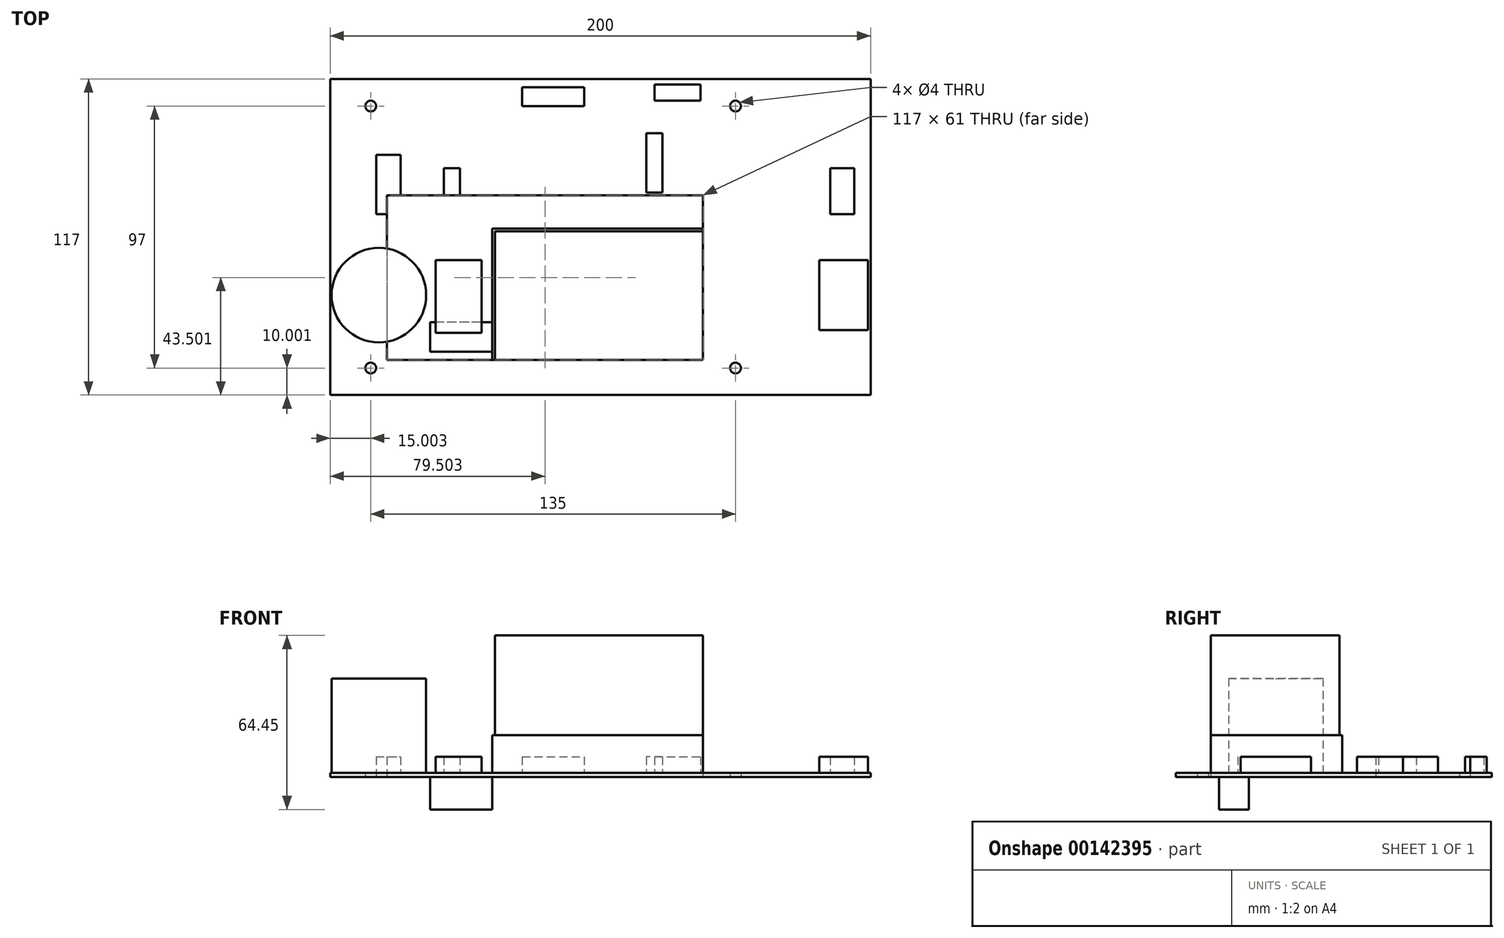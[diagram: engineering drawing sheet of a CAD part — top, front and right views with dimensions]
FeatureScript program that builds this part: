
annotation { "Feature Type Name" : "Feature", "Feature Type Description" : "" }
export const myFeature = defineFeature(function(context is Context, id is Id, definition is map)
    precondition{}
    {
        {
            var Q0;
            Q0=qCreatedBy(makeId("Top.planeOp"),FACE);
            var sketch = newSketch(context, id + "F0", { "sketchPlane" : qUnion([Q0])});
            skLineSegment(sketch, "E0.bottom", {"start": v(-88.8, 43.67) * mm, "end": v(111.2, 43.67) * mm});
            skLineSegment(sketch, "E0.top", {"start": v(-88.8, -73.33) * mm, "end": v(111.2, -73.33) * mm});
            skLineSegment(sketch, "E0.left", {"start": v(-88.8, 43.67) * mm, "end": v(-88.8, -73.33) * mm});
            skLineSegment(sketch, "E0.right", {"start": v(111.2, 43.67) * mm, "end": v(111.2, -73.33) * mm});
            skCircle(sketch, "E1", {"center": v(61.2, 33.67) * mm, "radius": 2 * mm});
            skCircle(sketch, "E2", {"center": v(61.2, -63.33) * mm, "radius": 2 * mm});
            skCircle(sketch, "E3", {"center": v(-73.8, -63.33) * mm, "radius": 2 * mm});
            skCircle(sketch, "E4", {"center": v(-73.8, 33.67) * mm, "radius": 2 * mm});
            skLineSegment(sketch, "E5.bottom", {"start": v(-67.8, 0.67) * mm, "end": v(49.2, 0.67) * mm});
            skLineSegment(sketch, "E5.top", {"start": v(-67.8, -60.33) * mm, "end": v(49.2, -60.33) * mm});
            skLineSegment(sketch, "E5.left", {"start": v(-67.8, 0.67) * mm, "end": v(-67.8, -60.33) * mm});
            skLineSegment(sketch, "E5.right", {"start": v(49.2, 0.67) * mm, "end": v(49.2, -60.33) * mm});
            skSolve(sketch);
        }
        {
            var Q0;
            Q0 = qSketchRegion(id + "F0", true);
            extrude(context, id + "F1", {"entities" : qUnion([Q0]), "depth" : 1.5 * mm});
        }
        {
            var Q0;
            Q0=makeQuery(id+"F1.opExtrude","CAP_FACE",FACE,{"disambiguationData":[OSD([sQuery(id+"F0.wireOp",EDGE,"E0.bottom"),sQuery(id+"F0.wireOp",EDGE,"E0.top"),sQuery(id+"F0.wireOp",EDGE,"E0.left"),sQuery(id+"F0.wireOp",EDGE,"E0.right"),sQuery(id+"F0.wireOp",EDGE,"E1"),sQuery(id+"F0.wireOp",EDGE,"E2"),sQuery(id+"F0.wireOp",EDGE,"E3"),sQuery(id+"F0.wireOp",EDGE,"E4")])],"isStart":false});
            var sketch = newSketch(context, id + "F2", { "sketchPlane" : qUnion([Q0])});
            skLineSegment(sketch, "E6.bottom", {"start": v(-17.8, 40.67) * mm, "end": v(5.2, 40.67) * mm});
            skLineSegment(sketch, "E6.top", {"start": v(-17.8, 33.67) * mm, "end": v(5.2, 33.67) * mm});
            skLineSegment(sketch, "E6.left", {"start": v(5.2, 40.67) * mm, "end": v(5.2, 33.67) * mm});
            skLineSegment(sketch, "E6.right", {"start": v(-17.8, 40.67) * mm, "end": v(-17.8, 33.67) * mm});
            skLineSegment(sketch, "E7.bottom", {"start": v(31.2, 41.67) * mm, "end": v(48.2, 41.67) * mm});
            skLineSegment(sketch, "E7.top", {"start": v(31.2, 35.67) * mm, "end": v(48.2, 35.67) * mm});
            skLineSegment(sketch, "E7.left", {"start": v(31.2, 41.67) * mm, "end": v(31.2, 35.67) * mm});
            skLineSegment(sketch, "E7.right", {"start": v(48.2, 41.67) * mm, "end": v(48.2, 35.67) * mm});
            skLineSegment(sketch, "E8.top", {"start": v(34.2, 1.67) * mm, "end": v(28.2, 1.67) * mm});
            skLineSegment(sketch, "E8.left", {"start": v(28.2, 23.67) * mm, "end": v(28.2, 1.67) * mm});
            skLineSegment(sketch, "E9", {"start": v(34.2, 23.67) * mm, "end": v(34.2, 1.67) * mm});
            skPoint(sketch, "E10.orphan", {"position": v(0, 1.67) * mm});
            skLineSegment(sketch, "E11", {"start": v(28.2, 23.67) * mm, "end": v(34.2, 23.67) * mm});
            skPoint(sketch, "E12.orphan", {"position": v(28.2, 0) * mm});
            skLineSegment(sketch, "E13.bottom", {"start": v(-49.8, -23.33) * mm, "end": v(-32.8, -23.33) * mm});
            skLineSegment(sketch, "E13.top", {"start": v(-49.8, -50.33) * mm, "end": v(-32.8, -50.33) * mm});
            skLineSegment(sketch, "E13.left", {"start": v(-49.8, -23.33) * mm, "end": v(-49.8, -50.33) * mm});
            skLineSegment(sketch, "E13.right", {"start": v(-32.8, -23.33) * mm, "end": v(-32.8, -50.33) * mm});
            skLineSegment(sketch, "E14.bottom", {"start": v(92.2, -23.33) * mm, "end": v(110.2, -23.33) * mm});
            skLineSegment(sketch, "E14.top", {"start": v(92.2, -49.33) * mm, "end": v(110.2, -49.33) * mm});
            skLineSegment(sketch, "E14.left", {"start": v(92.2, -23.33) * mm, "end": v(92.2, -49.33) * mm});
            skLineSegment(sketch, "E14.right", {"start": v(110.2, -23.33) * mm, "end": v(110.2, -49.33) * mm});
            skCircle(sketch, "E15", {"center": v(-70.8, -36.33) * mm, "radius": 17.5 * mm});
            skLineSegment(sketch, "E16.bottom", {"start": v(-71.8, 15.67) * mm, "end": v(-62.8, 15.67) * mm});
            skLineSegment(sketch, "E16.top", {"start": v(-71.8, -6.33) * mm, "end": v(-62.8, -6.33) * mm});
            skLineSegment(sketch, "E16.left", {"start": v(-71.8, 15.67) * mm, "end": v(-71.8, -6.33) * mm});
            skLineSegment(sketch, "E16.right", {"start": v(-62.8, 15.67) * mm, "end": v(-62.8, -6.33) * mm});
            skLineSegment(sketch, "E17.bottom", {"start": v(96.2, 10.67) * mm, "end": v(105.2, 10.67) * mm});
            skLineSegment(sketch, "E17.top", {"start": v(96.2, -6.33) * mm, "end": v(105.2, -6.33) * mm});
            skLineSegment(sketch, "E17.left", {"start": v(96.2, 10.67) * mm, "end": v(96.2, -6.33) * mm});
            skLineSegment(sketch, "E17.right", {"start": v(105.2, 10.67) * mm, "end": v(105.2, -6.33) * mm});
            skLineSegment(sketch, "E18.bottom", {"start": v(-46.8, 10.67) * mm, "end": v(-40.8, 10.67) * mm});
            skLineSegment(sketch, "E18.top", {"start": v(-46.8, -1.33) * mm, "end": v(-40.8, -1.33) * mm});
            skLineSegment(sketch, "E18.left", {"start": v(-46.8, 10.67) * mm, "end": v(-46.8, -1.33) * mm});
            skLineSegment(sketch, "E18.right", {"start": v(-40.8, 10.67) * mm, "end": v(-40.8, -1.33) * mm});
            skSolve(sketch);
        }
        {
            var Q0;
            Q0=makeQuery(id+"F2.imprint","IMPRINT",FACE,{"disambiguationData":[TD([[makeQuery(id+"F2.imprint","IMPRINT",EDGE,{"derivedFrom":sQuery(id+"F2.wireOp",EDGE,"E6.bottom")}),-1.0]])]});
            var Q1;
            Q1=makeQuery(id+"F2.imprint","IMPRINT",FACE,{"disambiguationData":[TD([[makeQuery(id+"F2.imprint","IMPRINT",EDGE,{"derivedFrom":sQuery(id+"F2.wireOp",EDGE,"E7.bottom")}),-1.0]])]});
            var Q2;
            Q2=makeQuery(id+"F2.imprint","IMPRINT",FACE,{"disambiguationData":[TD([[makeQuery(id+"F2.imprint","IMPRINT",EDGE,{"derivedFrom":sQuery(id+"F2.wireOp",EDGE,"E8.top")}),-1.0]])]});
            var Q3;
            Q3=makeQuery(id+"F2.imprint","IMPRINT",FACE,{"disambiguationData":[TD([[makeQuery(id+"F2.imprint","IMPRINT",EDGE,{"derivedFrom":sQuery(id+"F2.wireOp",EDGE,"E14.bottom")}),-1.0]])]});
            var Q4;
            Q4=makeQuery(id+"F2.imprint","IMPRINT",FACE,{"disambiguationData":[TD([[makeQuery(id+"F2.imprint","IMPRINT",EDGE,{"derivedFrom":sQuery(id+"F2.wireOp",EDGE,"E13.bottom")}),-1.0]])]});
            var Q5;
            Q5=makeQuery(id+"F2.imprint","IMPRINT",FACE,{"disambiguationData":[TD([[makeQuery(id+"F2.imprint","IMPRINT",EDGE,{"derivedFrom":sQuery(id+"F2.wireOp",EDGE,"E16.bottom")}),-1.0]])]});
            var Q6;
            Q6=makeQuery(id+"F2.imprint","IMPRINT",FACE,{"disambiguationData":[TD([[makeQuery(id+"F2.imprint","IMPRINT",EDGE,{"derivedFrom":sQuery(id+"F2.wireOp",EDGE,"E17.bottom")}),-1.0]])]});
            var Q7;
            Q7=makeQuery(id+"F2.imprint","IMPRINT",FACE,{"disambiguationData":[TD([[makeQuery(id+"F2.imprint","IMPRINT",EDGE,{"derivedFrom":sQuery(id+"F2.wireOp",EDGE,"E18.bottom")}),-1.0]])]});
            extrude(context, id + "F3", {"entities" : qUnion([Q0, Q1, Q2, Q3, Q4, Q5, Q6, Q7]), "depth" : 6 * mm});
        }
        {
            var Q0;
            Q0=makeQuery(id+"F2.imprint","IMPRINT",FACE,{"disambiguationData":[TD([[makeQuery(id+"F2.imprint","IMPRINT",EDGE,{"derivedFrom":sQuery(id+"F2.wireOp",EDGE,"E15")}),1.0]])]});
            extrude(context, id + "F4", {"entities" : qUnion([Q0]), "depth" : 35 * mm});
        }
        {
            var Q0;
            Q0=makeQuery(id+"F1.opExtrude","CAP_FACE",FACE,{"disambiguationData":[OSD([sQuery(id+"F0.wireOp",EDGE,"E0.bottom"),sQuery(id+"F0.wireOp",EDGE,"E0.top"),sQuery(id+"F0.wireOp",EDGE,"E0.left"),sQuery(id+"F0.wireOp",EDGE,"E0.right"),sQuery(id+"F0.wireOp",EDGE,"E1"),sQuery(id+"F0.wireOp",EDGE,"E2"),sQuery(id+"F0.wireOp",EDGE,"E3"),sQuery(id+"F0.wireOp",EDGE,"E4")])],"isStart":false});
            var sketch = newSketch(context, id + "F5", { "sketchPlane" : qUnion([Q0])});
            skLineSegment(sketch, "E19.bottom", {"start": v(-28.8, -11.73) * mm, "end": v(88, -11.73) * mm});
            skLineSegment(sketch, "E19.top", {"start": v(-28.8, -72.73) * mm, "end": v(88, -72.73) * mm});
            skLineSegment(sketch, "E19.left", {"start": v(-28.8, -11.73) * mm, "end": v(-28.8, -72.73) * mm});
            skLineSegment(sketch, "E19.right", {"start": v(88, -11.73) * mm, "end": v(88, -72.73) * mm});
            skSolve(sketch);
        }
        {
            var Q0;
            Q0=makeQuery(id+"F5.imprint","IMPRINT",FACE,{"disambiguationData":[TD([[makeQuery(id+"F5.imprint","IMPRINT",EDGE,{"derivedFrom":sQuery(id+"F5.wireOp",EDGE,"E19.bottom")}),-1.0]])]});
            extrude(context, id + "F6", {"entities" : qUnion([Q0]), "depth" : 13.95 * mm});
        }
        {
            var Q0;
            Q0=makeQuery(id+"F6.opExtrude","CAP_FACE",FACE,{"disambiguationData":[OSD([sQuery(id+"F5.wireOp",EDGE,"E19.bottom"),sQuery(id+"F5.wireOp",EDGE,"E19.top"),sQuery(id+"F5.wireOp",EDGE,"E19.left"),sQuery(id+"F5.wireOp",EDGE,"E19.right")])],"isStart":false});
            var sketch = newSketch(context, id + "F7", { "sketchPlane" : qUnion([Q0])});
            skLineSegment(sketch, "E20.bottom", {"start": v(-27.8, -12.73) * mm, "end": v(87, -12.73) * mm});
            skLineSegment(sketch, "E20.top", {"start": v(-27.8, -71.73) * mm, "end": v(87, -71.73) * mm});
            skLineSegment(sketch, "E20.left", {"start": v(-27.8, -12.73) * mm, "end": v(-27.8, -71.73) * mm});
            skLineSegment(sketch, "E20.right", {"start": v(87, -12.73) * mm, "end": v(87, -71.73) * mm});
            skSolve(sketch);
        }
        {
            var Q0;
            Q0=makeQuery(id+"F7.imprint","IMPRINT",FACE,{"disambiguationData":[TD([[makeQuery(id+"F7.imprint","IMPRINT",EDGE,{"derivedFrom":sQuery(id+"F7.wireOp",EDGE,"E20.bottom")}),-1.0]])]});
            extrude(context, id + "F8", {"entities" : qUnion([Q0]), "depth" : 37 * mm});
        }
        {
            var Q0;
            Q0=makeQuery(id+"F1.opExtrude","CAP_FACE",FACE,{"disambiguationData":[OSD([sQuery(id+"F0.wireOp",EDGE,"E0.bottom"),sQuery(id+"F0.wireOp",EDGE,"E0.top"),sQuery(id+"F0.wireOp",EDGE,"E0.left"),sQuery(id+"F0.wireOp",EDGE,"E0.right"),sQuery(id+"F0.wireOp",EDGE,"E1"),sQuery(id+"F0.wireOp",EDGE,"E2"),sQuery(id+"F0.wireOp",EDGE,"E3"),sQuery(id+"F0.wireOp",EDGE,"E4")])],"isStart":true});
            var sketch = newSketch(context, id + "F9", { "sketchPlane" : qUnion([Q0])});
            skLineSegment(sketch, "E21.bottom", {"start": v(-28.8, 46.33) * mm, "end": v(-51.8, 46.33) * mm});
            skLineSegment(sketch, "E21.top", {"start": v(-28.8, 57.33) * mm, "end": v(-51.8, 57.33) * mm});
            skLineSegment(sketch, "E21.left", {"start": v(-28.8, 46.33) * mm, "end": v(-28.8, 57.33) * mm});
            skLineSegment(sketch, "E21.right", {"start": v(-51.8, 46.33) * mm, "end": v(-51.8, 57.33) * mm});
            skSolve(sketch);
        }
        {
            var Q0;
            Q0 = qSketchRegion(id + "F9", true);
            var Q1;
            Q1=makeQuery(id+"F9.imprint","IMPRINT",FACE,{"disambiguationData":[TD([[makeQuery(id+"F9.imprint","IMPRINT",EDGE,{"derivedFrom":sQuery(id+"F9.wireOp",EDGE,"E21.bottom")}),-1.0]])]});
            extrude(context, id + "F10", {"entities" : qUnion([Q0, Q1]), "depth" : 12 * mm});
        }
    });
